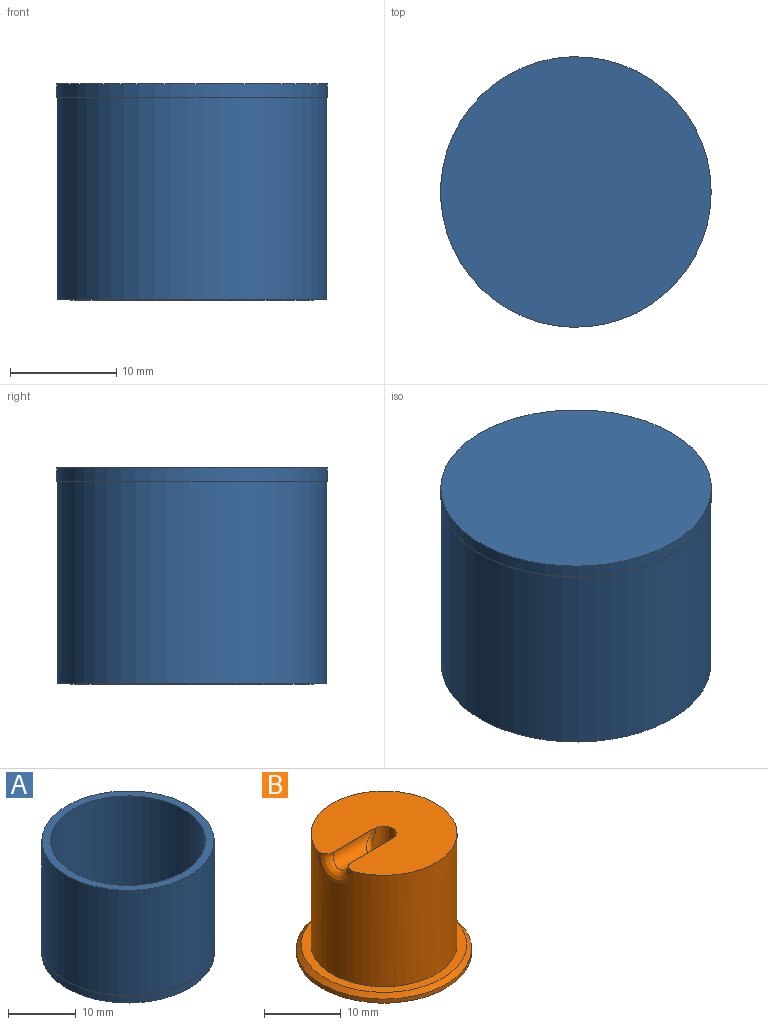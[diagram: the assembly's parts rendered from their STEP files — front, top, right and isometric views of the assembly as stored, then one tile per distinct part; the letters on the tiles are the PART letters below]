
ASSEMBLY  parts=2 mates=1
PART A: 7 faces, bbox 25.5x25.5x20.3 mm
  f0: cylinder r=11.43mm len=22.86mm, axis (0,0,-1), area 1368.1mm2, adj f2,f6
  f1: cylinder r=12.7mm len=25.4mm, axis (0,0,-1), area 1520.1mm2, adj f2,f3
  f2: plane 25.4x25.4mm, normal (0,0,1), area 96.3mm2, adj f0,f1
  f3: plane 25.49x25.49mm, normal (0,0,1), area 3.6mm2, adj f1,f5
  f4: plane 25.49x25.49mm, normal (0,0,-1), area 510.3mm2, adj f5
  f5: cylinder r=12.74mm len=25.49mm, axis (0,0,1), area 101.7mm2, adj f3,f4
  f6: plane 22.86x22.86mm, normal (0,0,1), area 410.4mm2, adj f0
PART B: 21 faces, bbox 22.9x22.9x19.7 mm
  f0: cylinder r=9.53mm len=19.05mm, axis (0,0,-1), area 1048.4mm2, adj f1,f14,f19
  f1: plane 19.05x18.52mm, normal (0,0,1), area 248.4mm2, adj f0,f2,f15,f16,f17,f19
  f2: cylinder r=1.59mm len=13.97mm, axis (0,0,-1), area 129.6mm2, adj f1,f8,f15,f16,f18
  f3: plane 22.86x22.86mm, normal (0,0,-1), area 244.4mm2, adj f8,f10,f12,f13
  f4: cylinder r=3.17mm len=14.99mm, axis (0,0,-1), area 287.6mm2, adj f5,f9,f10
  f5: cone r=0mm half-angle=59deg, axis (0,0,-1), area 36.9mm2, adj f4
  f6: cylinder r=3.17mm len=14.99mm, axis (0,0,-1), area 287.6mm2, adj f7,f11,f12
  f7: cone r=0mm half-angle=59deg, axis (0,0,-1), area 36.9mm2, adj f6
  f8: torus R=6.67mm, axis (0,0,1), area 115.6mm2, adj f2,f3,f9,f11
  f9: bspline ~6.86x4.56mm, area 6mm2, adj f4,f8,f10
  f10: torus R=3.43mm, axis (0,0,1), area 4mm2, adj f3,f4,f9
  f11: bspline ~6.86x4.53mm, area 6mm2, adj f6,f8,f12
  f12: torus R=3.43mm, axis (0,0,1), area 4mm2, adj f3,f6,f11
  f13: cylinder r=11.43mm len=22.86mm, axis (0,0,-1), area 45.6mm2, adj f3,f20
  f14: plane 21.59x21.59mm, normal (0,0,1), area 81.1mm2, adj f0,f20
  f15: plane 0.6x0.06mm, normal (-1,0,0), area 0mm2, adj f1,f2,f17,f18
  f16: plane 0.6x0.06mm, normal (-1,0,0), area 0mm2, adj f1,f2,f17,f18
  f17: cylinder r=1.65mm len=8.26mm, axis (-1,0,0), area 32.5mm2, adj f1,f15,f16,f18,f19
  f18: bspline ~3.23x2.95mm, area 7.6mm2, adj f2,f15,f16,f17
  f19: bspline ~6.75x3.53mm, area 15.5mm2, adj f0,f1,f17
  f20: cone r=11.43mm half-angle=45deg, axis (0,0,-1), area 62.7mm2, adj f13,f14
PLACE A rot(axis=(1,0,0),180deg) t=(-35.51,-36.11,1.34)mm
PLACE B rot(axis=(0,0,1),0deg) t=(-35.51,-36.11,-17.75)mm
MATE cylindrical A.f0 <-> B.f0  axis (0,0,-1) through (-35.51,-36.11,-17.71)mm
